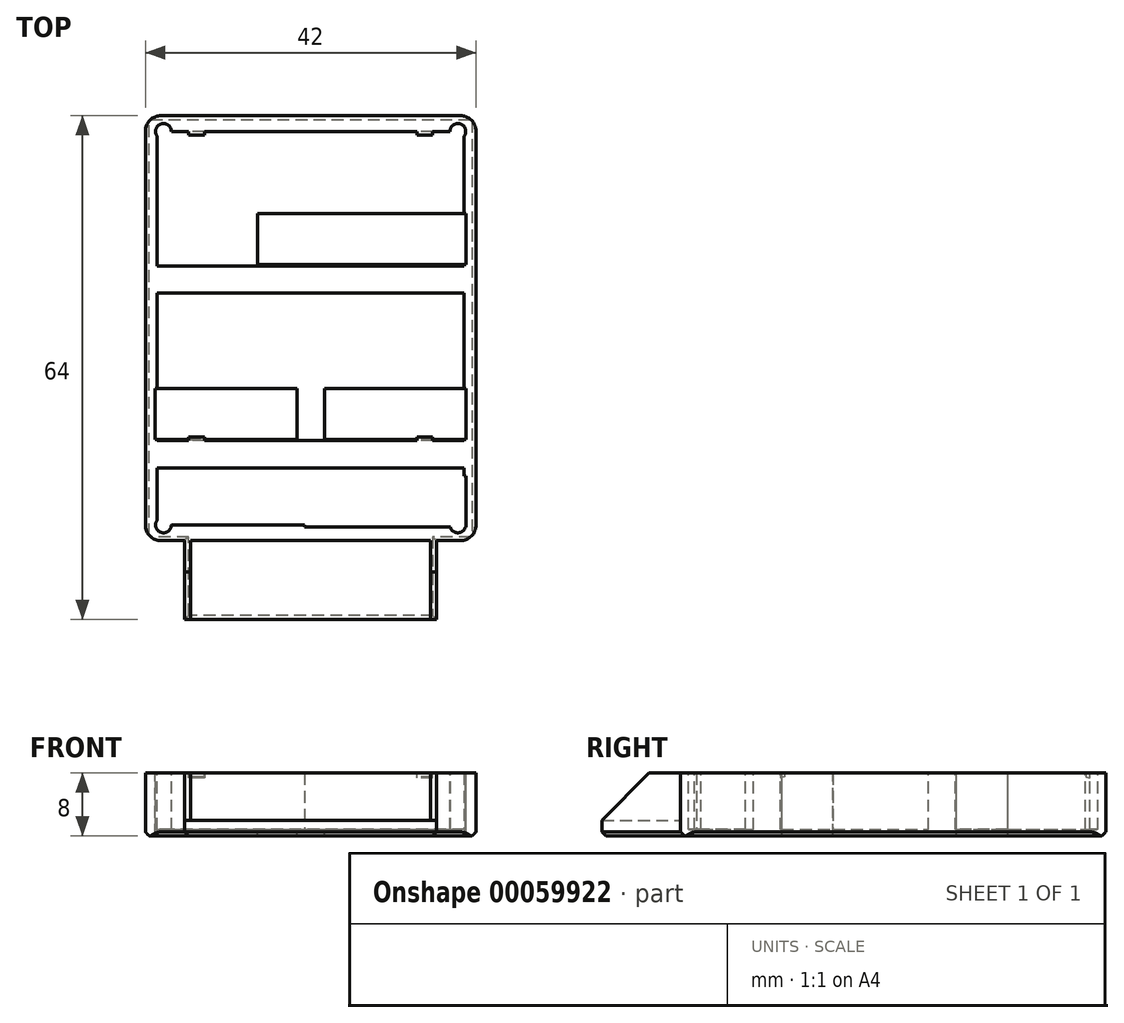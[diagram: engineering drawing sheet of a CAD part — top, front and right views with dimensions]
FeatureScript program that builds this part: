
annotation { "Feature Type Name" : "Feature", "Feature Type Description" : "" }
export const myFeature = defineFeature(function(context is Context, id is Id, definition is map)
    precondition{}
    {
        {
            var Q0;
            Q0=qCreatedBy(makeId("Top.planeOp"),FACE);
            var sketch = newSketch(context, id + "F0", { "sketchPlane" : qUnion([Q0])});
            skLineSegment(sketch, "E0.bottom", {"start": v(-21, 0) * mm, "end": v(21, 0) * mm});
            skLineSegment(sketch, "E0.top", {"start": v(-21, 54) * mm, "end": v(21, 54) * mm});
            skLineSegment(sketch, "E0.left", {"start": v(-21, 0) * mm, "end": v(-21, 54) * mm});
            skLineSegment(sketch, "E0.right", {"start": v(21, 0) * mm, "end": v(21, 54) * mm});
            skSolve(sketch);
        }
        {
            var Q0;
            Q0=makeQuery(id+"F0.imprint","IMPRINT",FACE,{"disambiguationData":[TD([[makeQuery(id+"F0.imprint","IMPRINT",EDGE,{"derivedFrom":sQuery(id+"F0.wireOp",EDGE,"E0.bottom")}),1.0]])]});
            extrude(context, id + "F1", {"entities" : qUnion([Q0]), "depth" : 8 * mm});
        }
        {
            var Q0;
            Q0=makeQuery(id+"F1.opExtrude","CAP_FACE",FACE,{"disambiguationData":[OSD([sQuery(id+"F0.wireOp",EDGE,"E0.bottom"),sQuery(id+"F0.wireOp",EDGE,"E0.top"),sQuery(id+"F0.wireOp",EDGE,"E0.left"),sQuery(id+"F0.wireOp",EDGE,"E0.right")])],"isStart":false});
            var sketch = newSketch(context, id + "F2", { "sketchPlane" : qUnion([Q0])});
            skLineSegment(sketch, "E1.bottom", {"start": v(-19.5, 2) * mm, "end": v(19.5, 2) * mm});
            skLineSegment(sketch, "E1.top", {"start": v(-19.5, 52) * mm, "end": v(19.5, 52) * mm});
            skLineSegment(sketch, "E1.left", {"start": v(-19.5, 2) * mm, "end": v(-19.5, 52) * mm});
            skLineSegment(sketch, "E1.right", {"start": v(19.5, 2) * mm, "end": v(19.5, 52) * mm});
            skLineSegment(sketch, "E2", {"start": v(0, 0) * mm, "end": v(0, 2) * mm, "construction": true});
            skLineSegment(sketch, "E3", {"start": v(21, 27) * mm, "end": v(19.5, 27) * mm, "construction": true});
            skSolve(sketch);
        }
        {
            var Q0;
            Q0 = qSketchRegion(id + "F2", true);
            extrude(context, id + "F3", {"entities" : qUnion([Q0]), "operationType" : NewBodyOperationType.REMOVE, "oppositeDirection" : true, "depth" : 7.2 * mm});
        }
        {
            var Q0;
            Q0=makeQuery(id+"F1.opExtrude","CAP_FACE",FACE,{"disambiguationData":[OSD([sQuery(id+"F0.wireOp",EDGE,"E0.bottom"),sQuery(id+"F0.wireOp",EDGE,"E0.top"),sQuery(id+"F0.wireOp",EDGE,"E0.left"),sQuery(id+"F0.wireOp",EDGE,"E0.right")])],"isStart":false});
            var sketch = newSketch(context, id + "F4", { "sketchPlane" : qUnion([Q0])});
            skPoint(sketch, "E4", {"position": v(-18.7, 52) * mm});
            skPoint(sketch, "E5", {"position": v(18.7, 52) * mm});
            skPoint(sketch, "E6", {"position": v(18.7, 2) * mm});
            skPoint(sketch, "E7", {"position": v(-18.7, 2) * mm});
            skCircle(sketch, "E8", {"center": v(-18.7, 52) * mm, "radius": 1 * mm});
            skCircle(sketch, "E9", {"center": v(18.7, 52) * mm, "radius": 1 * mm});
            skCircle(sketch, "E10", {"center": v(18.7, 2) * mm, "radius": 1 * mm});
            skCircle(sketch, "E11", {"center": v(-18.7, 2) * mm, "radius": 1 * mm});
            skSolve(sketch);
        }
        {
            var Q0;
            {var subQ0=sQuery(id+"F4.wireOp",EDGE,"E8");var subQ1=makeQuery(id+"F3.boolean.opBoolean","COPY",EDGE,{"derivedFrom":makeQuery(id+"F3.opExtrude","CAP_EDGE",EDGE,{"disambiguationData":[OSD([sQuery(id+"F2.wireOp",EDGE,"E1.top")])],"isStart":true})});var subQ2=makeQuery(id+"F4.imprint","INTERSECT",VERTEX,{"derivedFrom":[subQ1,subQ0]});Q0=makeQuery(id+"F4.imprint","IMPRINT",FACE,{"disambiguationData":[TD([[makeQuery(id+"F4.imprint","IMPRINT",EDGE,{"disambiguationData":[TD([[subQ2,-1.0]])],"derivedFrom":subQ0}),1.0]])]});}
            var Q1;
            {var subQ0=sQuery(id+"F4.wireOp",EDGE,"E8");var subQ1=makeQuery(id+"F3.boolean.opBoolean","COPY",EDGE,{"derivedFrom":makeQuery(id+"F3.opExtrude","CAP_EDGE",EDGE,{"disambiguationData":[OSD([sQuery(id+"F2.wireOp",EDGE,"E1.top")])],"isStart":true})});var subQ2=makeQuery(id+"F4.imprint","INTERSECT",VERTEX,{"derivedFrom":[subQ1,subQ0]});Q1=makeQuery(id+"F4.imprint","IMPRINT",FACE,{"disambiguationData":[TD([[makeQuery(id+"F4.imprint","IMPRINT",EDGE,{"disambiguationData":[TD([[subQ2,1.0]])],"derivedFrom":subQ0}),1.0]])]});}
            var Q2;
            {var subQ0=sQuery(id+"F4.wireOp",EDGE,"E9");var subQ1=makeQuery(id+"F3.boolean.opBoolean","COPY",EDGE,{"derivedFrom":makeQuery(id+"F3.opExtrude","CAP_EDGE",EDGE,{"disambiguationData":[OSD([sQuery(id+"F2.wireOp",EDGE,"E1.top")])],"isStart":true})});var subQ2=makeQuery(id+"F4.imprint","INTERSECT",VERTEX,{"derivedFrom":[subQ1,subQ0]});Q2=makeQuery(id+"F4.imprint","IMPRINT",FACE,{"disambiguationData":[TD([[makeQuery(id+"F4.imprint","IMPRINT",EDGE,{"disambiguationData":[TD([[subQ2,-1.0]])],"derivedFrom":subQ0}),1.0]])]});}
            var Q3;
            {var subQ0=sQuery(id+"F4.wireOp",EDGE,"E9");var subQ1=makeQuery(id+"F3.boolean.opBoolean","COPY",EDGE,{"derivedFrom":makeQuery(id+"F3.opExtrude","CAP_EDGE",EDGE,{"disambiguationData":[OSD([sQuery(id+"F2.wireOp",EDGE,"E1.top")])],"isStart":true})});var subQ2=makeQuery(id+"F4.imprint","INTERSECT",VERTEX,{"derivedFrom":[subQ1,subQ0]});Q3=makeQuery(id+"F4.imprint","IMPRINT",FACE,{"disambiguationData":[TD([[makeQuery(id+"F4.imprint","IMPRINT",EDGE,{"disambiguationData":[TD([[subQ2,1.0]])],"derivedFrom":subQ0}),1.0]])]});}
            var Q4;
            {var subQ0=sQuery(id+"F4.wireOp",EDGE,"E10");var subQ1=makeQuery(id+"F3.boolean.opBoolean","COPY",EDGE,{"derivedFrom":makeQuery(id+"F3.opExtrude","CAP_EDGE",EDGE,{"disambiguationData":[OSD([sQuery(id+"F2.wireOp",EDGE,"E1.bottom")])],"isStart":true})});var subQ2=makeQuery(id+"F4.imprint","INTERSECT",VERTEX,{"derivedFrom":[subQ1,subQ0]});Q4=makeQuery(id+"F4.imprint","IMPRINT",FACE,{"disambiguationData":[TD([[makeQuery(id+"F4.imprint","IMPRINT",EDGE,{"disambiguationData":[TD([[subQ2,1.0]])],"derivedFrom":subQ0}),1.0]])]});}
            var Q5;
            {var subQ0=sQuery(id+"F4.wireOp",EDGE,"E11");var subQ1=makeQuery(id+"F3.boolean.opBoolean","COPY",EDGE,{"derivedFrom":makeQuery(id+"F3.opExtrude","CAP_EDGE",EDGE,{"disambiguationData":[OSD([sQuery(id+"F2.wireOp",EDGE,"E1.bottom")])],"isStart":true})});var subQ2=makeQuery(id+"F4.imprint","INTERSECT",VERTEX,{"derivedFrom":[subQ1,subQ0]});Q5=makeQuery(id+"F4.imprint","IMPRINT",FACE,{"disambiguationData":[TD([[makeQuery(id+"F4.imprint","IMPRINT",EDGE,{"disambiguationData":[TD([[subQ2,-1.0]])],"derivedFrom":subQ0}),1.0]])]});}
            var Q6;
            {var subQ0=sQuery(id+"F4.wireOp",EDGE,"E11");var subQ1=makeQuery(id+"F3.boolean.opBoolean","COPY",EDGE,{"derivedFrom":makeQuery(id+"F3.opExtrude","CAP_EDGE",EDGE,{"disambiguationData":[OSD([sQuery(id+"F2.wireOp",EDGE,"E1.bottom")])],"isStart":true})});var subQ2=makeQuery(id+"F4.imprint","INTERSECT",VERTEX,{"derivedFrom":[subQ1,subQ0]});Q6=makeQuery(id+"F4.imprint","IMPRINT",FACE,{"disambiguationData":[TD([[makeQuery(id+"F4.imprint","IMPRINT",EDGE,{"disambiguationData":[TD([[subQ2,1.0]])],"derivedFrom":subQ0}),1.0]])]});}
            var Q7;
            {var subQ0=sQuery(id+"F4.wireOp",EDGE,"E10");var subQ1=makeQuery(id+"F3.boolean.opBoolean","COPY",EDGE,{"derivedFrom":makeQuery(id+"F3.opExtrude","CAP_EDGE",EDGE,{"disambiguationData":[OSD([sQuery(id+"F2.wireOp",EDGE,"E1.bottom")])],"isStart":true})});var subQ2=makeQuery(id+"F4.imprint","INTERSECT",VERTEX,{"derivedFrom":[subQ1,subQ0]});Q7=makeQuery(id+"F4.imprint","IMPRINT",FACE,{"disambiguationData":[TD([[makeQuery(id+"F4.imprint","IMPRINT",EDGE,{"disambiguationData":[TD([[subQ2,-1.0]])],"derivedFrom":subQ0}),1.0]])]});}
            var Q8;
            Q8=makeQuery(id+"F3.boolean.opBoolean","COPY",FACE,{"derivedFrom":makeQuery(id+"F3.opExtrude","CAP_FACE",FACE,{"disambiguationData":[OSD([sQuery(id+"F2.wireOp",EDGE,"E1.bottom"),sQuery(id+"F2.wireOp",EDGE,"E1.top"),sQuery(id+"F2.wireOp",EDGE,"E1.left"),sQuery(id+"F2.wireOp",EDGE,"E1.right")])],"isStart":false})});
            extrude(context, id + "F5", {"entities" : qUnion([Q0, Q1, Q2, Q3, Q4, Q5, Q6, Q7]), "operationType" : NewBodyOperationType.REMOVE, "endBound" : BoundingType.UP_TO_SURFACE, "oppositeDirection" : true, "endBoundEntityFace" : qUnion([Q8]), "depth" : 25 * mm});
        }
        {
            var Q0;
            Q0=makeQuery(id+"F1.opExtrude","CAP_FACE",FACE,{"disambiguationData":[OSD([sQuery(id+"F0.wireOp",EDGE,"E0.bottom"),sQuery(id+"F0.wireOp",EDGE,"E0.top"),sQuery(id+"F0.wireOp",EDGE,"E0.left"),sQuery(id+"F0.wireOp",EDGE,"E0.right")])],"isStart":false});
            var sketch = newSketch(context, id + "F6", { "sketchPlane" : qUnion([Q0])});
            skLineSegment(sketch, "E12.bottom", {"start": v(-0.75, 8.25) * mm, "end": v(19.75, 8.25) * mm});
            skLineSegment(sketch, "E12.top", {"start": v(-0.75, 1.75) * mm, "end": v(19.75, 1.75) * mm});
            skLineSegment(sketch, "E12.left", {"start": v(-0.75, 8.25) * mm, "end": v(-0.75, 1.75) * mm});
            skLineSegment(sketch, "E12.right", {"start": v(19.75, 8.25) * mm, "end": v(19.75, 1.75) * mm});
            skLineSegment(sketch, "E13.bottom", {"start": v(19.75, 12.85) * mm, "end": v(1.75, 12.85) * mm});
            skLineSegment(sketch, "E13.top", {"start": v(19.75, 19.35) * mm, "end": v(1.75, 19.35) * mm});
            skLineSegment(sketch, "E13.left", {"start": v(19.75, 12.85) * mm, "end": v(19.75, 19.35) * mm});
            skLineSegment(sketch, "E13.right", {"start": v(1.75, 12.85) * mm, "end": v(1.75, 19.35) * mm});
            skLineSegment(sketch, "E14", {"start": v(19.75, 8.25) * mm, "end": v(19.75, 12.85) * mm, "construction": true});
            skLineSegment(sketch, "E15", {"start": v(0, 0) * mm, "end": v(0, 22.3) * mm, "construction": true});
            skLineSegment(sketch, "E16.MirrorCS", {"start": v(-19.75, 12.85) * mm, "end": v(-1.75, 12.85) * mm});
            skLineSegment(sketch, "E17.MirrorCS", {"start": v(-19.75, 19.35) * mm, "end": v(-1.75, 19.35) * mm});
            skLineSegment(sketch, "E18.MirrorCS", {"start": v(-19.75, 12.85) * mm, "end": v(-19.75, 19.35) * mm});
            skLineSegment(sketch, "E19.MirrorCS", {"start": v(-1.75, 12.85) * mm, "end": v(-1.75, 19.35) * mm});
            skLineSegment(sketch, "E20.bottom", {"start": v(19.75, 41.55) * mm, "end": v(-6.75, 41.55) * mm});
            skLineSegment(sketch, "E20.top", {"start": v(19.75, 35.05) * mm, "end": v(-6.75, 35.05) * mm});
            skLineSegment(sketch, "E20.left", {"start": v(19.75, 41.55) * mm, "end": v(19.75, 35.05) * mm});
            skLineSegment(sketch, "E20.right", {"start": v(-6.75, 41.55) * mm, "end": v(-6.75, 35.05) * mm});
            skLineSegment(sketch, "E21", {"start": v(19.75, 19.35) * mm, "end": v(19.75, 35.05) * mm, "construction": true});
            skSolve(sketch);
        }
        {
            var Q0;
            Q0 = qSketchRegion(id + "F6", true);
            extrude(context, id + "F7", {"entities" : qUnion([Q0]), "operationType" : NewBodyOperationType.REMOVE, "endBound" : BoundingType.THROUGH_ALL, "oppositeDirection" : true, "depth" : 25 * mm});
        }
        {
            var Q0;
            Q0=makeQuery(id+"F1.opExtrude","SWEPT_FACE",FACE,{"disambiguationData":[OSD([sQuery(id+"F0.wireOp",EDGE,"E0.bottom")])]});
            var sketch = newSketch(context, id + "F8", { "sketchPlane" : qUnion([Q0])});
            skLineSegment(sketch, "E22", {"start": v(-15.25, 8) * mm, "end": v(-15.25, 2) * mm});
            skLineSegment(sketch, "E23", {"start": v(-15.25, 2) * mm, "end": v(15.25, 2) * mm});
            skLineSegment(sketch, "E24", {"start": v(15.25, 2) * mm, "end": v(15.25, 8) * mm});
            skLineSegment(sketch, "E25", {"start": v(0, 0) * mm, "end": v(0, 2) * mm, "construction": true});
            skLineSegment(sketch, "E26", {"start": v(-15.25, 8) * mm, "end": v(-16, 8) * mm});
            skLineSegment(sketch, "E27", {"start": v(-16, 8) * mm, "end": v(-16, 0) * mm});
            skLineSegment(sketch, "E28", {"start": v(-16, 0) * mm, "end": v(16, 0) * mm});
            skLineSegment(sketch, "E29", {"start": v(16, 0) * mm, "end": v(16, 8) * mm});
            skLineSegment(sketch, "E30", {"start": v(16, 8) * mm, "end": v(15.25, 8) * mm});
            skSolve(sketch);
        }
        {
            var Q0;
            Q0 = qSketchRegion(id + "F8", true);
            extrude(context, id + "F9", {"entities" : qUnion([Q0]), "operationType" : NewBodyOperationType.ADD, "depth" : 10 * mm});
        }
        {
            var Q0;
            Q0=makeQuery(id+"F9.opExtrude","SWEPT_EDGE",EDGE,{"disambiguationData":[OSD([sQuery(id+"F0.wireOp",EDGE,"E0.bottom"),sQuery(id+"F8.wireOp",EDGE,"E28"),sQuery(id+"F8.wireOp",EDGE,"E29")])]});
            var Q1;
            {var subQ0=sQuery(id+"F0.wireOp",EDGE,"E0.right");var subQ1=sQuery(id+"F0.wireOp",EDGE,"E0.bottom");Q1=makeQuery(id+"F9.boolean.opBoolean","SPLIT",EDGE,{"disambiguationData":[TD([makeQuery(id+"F1.opExtrude","SWEPT_FACE",FACE,{"disambiguationData":[OSD([subQ0])]})])],"derivedFrom":makeQuery(id+"F1.opExtrude","CAP_EDGE",EDGE,{"disambiguationData":[OSD([subQ1])],"isStart":true})});}
            var Q2;
            Q2=makeQuery(id+"F1.opExtrude","CAP_EDGE",EDGE,{"disambiguationData":[OSD([sQuery(id+"F0.wireOp",EDGE,"E0.right")])],"isStart":true});
            var Q3;
            Q3=makeQuery(id+"F9.opExtrude","SWEPT_EDGE",EDGE,{"disambiguationData":[OSD([sQuery(id+"F0.wireOp",EDGE,"E0.bottom"),sQuery(id+"F8.wireOp",EDGE,"E27"),sQuery(id+"F8.wireOp",EDGE,"E28")])]});
            var Q4;
            {var subQ0=sQuery(id+"F0.wireOp",EDGE,"E0.left");var subQ1=sQuery(id+"F0.wireOp",EDGE,"E0.bottom");Q4=makeQuery(id+"F9.boolean.opBoolean","SPLIT",EDGE,{"disambiguationData":[TD([makeQuery(id+"F1.opExtrude","SWEPT_FACE",FACE,{"disambiguationData":[OSD([subQ0])]})])],"derivedFrom":makeQuery(id+"F1.opExtrude","CAP_EDGE",EDGE,{"disambiguationData":[OSD([subQ1])],"isStart":true})});}
            var Q5;
            Q5=makeQuery(id+"F1.opExtrude","CAP_EDGE",EDGE,{"disambiguationData":[OSD([sQuery(id+"F0.wireOp",EDGE,"E0.left")])],"isStart":true});
            var Q6;
            Q6=makeQuery(id+"F1.opExtrude","CAP_EDGE",EDGE,{"disambiguationData":[OSD([sQuery(id+"F0.wireOp",EDGE,"E0.top")])],"isStart":true});
            var Q7;
            Q7=makeQuery(id+"F9.opExtrude","CAP_EDGE",EDGE,{"disambiguationData":[OSD([sQuery(id+"F8.wireOp",EDGE,"E28")])],"isStart":false});
            chamfer(context, id + "F10", {"entities" : qUnion([Q0, Q1, Q2, Q3, Q4, Q5, Q6, Q7]), "width" : 0.5 * mm, "tangentPropagation" : true});
        }
        {
            var Q0;
            Q0=makeQuery(id+"F1.opExtrude","SWEPT_EDGE",EDGE,{"disambiguationData":[OSD([sQuery(id+"F0.wireOp",EDGE,"E0.bottom"),sQuery(id+"F0.wireOp",EDGE,"E0.right")])]});
            var Q1;
            Q1=makeQuery(id+"F1.opExtrude","SWEPT_EDGE",EDGE,{"disambiguationData":[OSD([sQuery(id+"F0.wireOp",EDGE,"E0.top"),sQuery(id+"F0.wireOp",EDGE,"E0.right")])]});
            var Q2;
            Q2=makeQuery(id+"F1.opExtrude","SWEPT_EDGE",EDGE,{"disambiguationData":[OSD([sQuery(id+"F0.wireOp",EDGE,"E0.bottom"),sQuery(id+"F0.wireOp",EDGE,"E0.left")])]});
            var Q3;
            Q3=makeQuery(id+"F1.opExtrude","SWEPT_EDGE",EDGE,{"disambiguationData":[OSD([sQuery(id+"F0.wireOp",EDGE,"E0.top"),sQuery(id+"F0.wireOp",EDGE,"E0.left")])]});
            fillet(context, id + "F11", {"entities" : qUnion([Q0, Q1, Q2, Q3]), "radius" : 2 * mm, "tangentPropagation" : true, "allowEdgeOverflow" : false});
        }
        {
            var Q0;
            Q0=makeQuery(id+"F9.boolean.opBoolean","MERGE",FACE,{"derivedFrom":[makeQuery(id+"F1.opExtrude","CAP_FACE",FACE,{"disambiguationData":[OSD([sQuery(id+"F0.wireOp",EDGE,"E0.bottom"),sQuery(id+"F0.wireOp",EDGE,"E0.top"),sQuery(id+"F0.wireOp",EDGE,"E0.left"),sQuery(id+"F0.wireOp",EDGE,"E0.right")])],"isStart":false}),makeQuery(id+"F9.opExtrude","SWEPT_FACE",FACE,{"disambiguationData":[OSD([sQuery(id+"F8.wireOp",EDGE,"E26")])]}),makeQuery(id+"F9.opExtrude","SWEPT_FACE",FACE,{"disambiguationData":[OSD([sQuery(id+"F8.wireOp",EDGE,"E30")])]})]});
            var sketch = newSketch(context, id + "F12", { "sketchPlane" : qUnion([Q0])});
            skLineSegment(sketch, "E31.bottom", {"start": v(-19.5, 9.25) * mm, "end": v(19.5, 9.25) * mm});
            skLineSegment(sketch, "E31.top", {"start": v(-19.5, 12.7) * mm, "end": v(19.5, 12.7) * mm});
            skLineSegment(sketch, "E31.left", {"start": v(-19.5, 9.25) * mm, "end": v(-19.5, 12.7) * mm});
            skLineSegment(sketch, "E31.right", {"start": v(19.5, 9.25) * mm, "end": v(19.5, 12.7) * mm});
            skLineSegment(sketch, "E32.bottom", {"start": v(19.5, 34.9) * mm, "end": v(-19.5, 34.9) * mm});
            skLineSegment(sketch, "E32.top", {"start": v(19.5, 31.45) * mm, "end": v(-19.5, 31.45) * mm});
            skLineSegment(sketch, "E32.left", {"start": v(19.5, 34.9) * mm, "end": v(19.5, 31.45) * mm});
            skLineSegment(sketch, "E32.right", {"start": v(-19.5, 34.9) * mm, "end": v(-19.5, 31.45) * mm});
            skSolve(sketch);
        }
        {
            var Q0;
            Q0=makeQuery(id+"F12.imprint","IMPRINT",FACE,{"disambiguationData":[TD([[makeQuery(id+"F12.imprint","IMPRINT",EDGE,{"derivedFrom":sQuery(id+"F12.wireOp",EDGE,"E31.bottom")}),1.0]])]});
            var Q1;
            Q1=makeQuery(id+"F12.imprint","IMPRINT",FACE,{"disambiguationData":[TD([[makeQuery(id+"F12.imprint","IMPRINT",EDGE,{"derivedFrom":sQuery(id+"F12.wireOp",EDGE,"E32.bottom")}),1.0]])]});
            var Q2;
            {var subQ0=sQuery(id+"F2.wireOp",EDGE,"E1.bottom");var subQ1=sQuery(id+"F4.wireOp",EDGE,"E8");var subQ2=sQuery(id+"F2.wireOp",EDGE,"E1.top");var subQ3=sQuery(id+"F4.wireOp",EDGE,"E11");var subQ4=sQuery(id+"F2.wireOp",EDGE,"E1.left");var subQ5=sQuery(id+"F4.wireOp",EDGE,"E9");var subQ6=sQuery(id+"F2.wireOp",EDGE,"E1.right");Q2=makeQuery(id+"F7.boolean.opBoolean","SPLIT",FACE,{"disambiguationData":[TD([makeQuery(id+"F3.boolean.opBoolean","COPY",FACE,{"derivedFrom":makeQuery(id+"F3.opExtrude","SWEPT_FACE",FACE,{"disambiguationData":[OSD([subQ0])]})})])],"derivedFrom":makeQuery(id+"F5.boolean.opBoolean","MERGE",FACE,{"derivedFrom":[makeQuery(id+"F3.boolean.opBoolean","COPY",FACE,{"derivedFrom":makeQuery(id+"F3.opExtrude","CAP_FACE",FACE,{"disambiguationData":[OSD([subQ0,subQ2,subQ4,subQ6])],"isStart":false})}),makeQuery(id+"F5.opExtrude","CAP_FACE",FACE,{"disambiguationData":[OSD([subQ1])],"isStart":false}),makeQuery(id+"F5.opExtrude","CAP_FACE",FACE,{"disambiguationData":[OSD([subQ5])],"isStart":false}),makeQuery(id+"F5.opExtrude","CAP_FACE",FACE,{"disambiguationData":[OSD([sQuery(id+"F4.wireOp",EDGE,"E10")])],"isStart":false}),makeQuery(id+"F5.opExtrude","CAP_FACE",FACE,{"disambiguationData":[OSD([subQ3])],"isStart":false})]})});}
            extrude(context, id + "F13", {"entities" : qUnion([Q0, Q1]), "operationType" : NewBodyOperationType.ADD, "endBound" : BoundingType.UP_TO_SURFACE, "oppositeDirection" : true, "endBoundEntityFace" : qUnion([Q2]), "offsetDistance" : 25 * mm, "depth" : 25 * mm});
        }
        {
            var Q0;
            {var subQ2=sQuery(id+"F4.wireOp",EDGE,"E8");var subQ3=makeQuery(id+"F5.boolean.opBoolean","COPY",FACE,{"derivedFrom":makeQuery(id+"F5.opExtrude","SWEPT_FACE",FACE,{"disambiguationData":[OSD([subQ2])]})});var subQ6=sQuery(id+"F2.wireOp",EDGE,"E1.left");Q0=makeQuery(id+"F13.boolean.opBoolean","SPLIT",FACE,{"disambiguationData":[TD([subQ3])],"derivedFrom":makeQuery(id+"F7.boolean.opBoolean","SPLIT",FACE,{"disambiguationData":[TD([subQ3])],"derivedFrom":makeQuery(id+"F3.boolean.opBoolean","COPY",FACE,{"derivedFrom":makeQuery(id+"F3.opExtrude","SWEPT_FACE",FACE,{"disambiguationData":[OSD([subQ6])]})})})});}
            cPlane(context, id + "F14", {"entities" : qUnion([Q0]), "cplaneType" : CPlaneType.OFFSET, "offset" : 5 * mm, "width" : 150 * mm, "height" : 150 * mm});
        }
        {
            var Q0;
            Q0=qCreatedBy(id+"F14.planeOp",FACE);
            var sketch = newSketch(context, id + "F15", { "sketchPlane" : qUnion([Q0])});
            skLineSegment(sketch, "E33", {"start": v(12.7, 8) * mm, "end": v(13.2, 8) * mm});
            skLineSegment(sketch, "E34", {"start": v(13.2, 8) * mm, "end": v(13.2, 7.5) * mm});
            skLineSegment(sketch, "E35", {"start": v(13.2, 7.5) * mm, "end": v(12.7, 7.37) * mm});
            skLineSegment(sketch, "E36", {"start": v(12.7, 7.37) * mm, "end": v(12.7, 8) * mm});
            skLineSegment(sketch, "E37", {"start": v(52, 8) * mm, "end": v(51.5, 8) * mm});
            skLineSegment(sketch, "E38", {"start": v(51.5, 8) * mm, "end": v(51.5, 7.5) * mm});
            skLineSegment(sketch, "E39", {"start": v(51.5, 7.5) * mm, "end": v(52, 7.37) * mm});
            skLineSegment(sketch, "E40", {"start": v(52, 7.37) * mm, "end": v(52, 8) * mm});
            skSolve(sketch);
        }
        {
            var Q0;
            Q0 = qSketchRegion(id + "F15", true);
            extrude(context, id + "F16", {"entities" : qUnion([Q0]), "operationType" : NewBodyOperationType.ADD, "endBound" : BoundingType.SYMMETRIC, "depth" : 2 * mm});
        }
        {
            var Q0;
            Q0=qCreatedBy(id+"F14.planeOp",FACE);
            cPlane(context, id + "F17", {"entities" : qUnion([Q0]), "cplaneType" : CPlaneType.OFFSET, "offset" : 29 * mm, "width" : 150 * mm, "height" : 150 * mm});
        }
        {
            var Q0;
            Q0=qCreatedBy(id+"F17.planeOp",FACE);
            var sketch = newSketch(context, id + "F18", { "sketchPlane" : qUnion([Q0])});
            skLineSegment(sketch, "E41.0.0", {"start": v(13.2, 8) * mm, "end": v(12.7, 8) * mm});
            skLineSegment(sketch, "E41.0.1", {"start": v(12.7, 8) * mm, "end": v(12.7, 7.37) * mm});
            skLineSegment(sketch, "E41.0.2", {"start": v(12.7, 7.37) * mm, "end": v(13.2, 7.5) * mm});
            skLineSegment(sketch, "E41.0.3", {"start": v(13.2, 7.5) * mm, "end": v(13.2, 8) * mm});
            skLineSegment(sketch, "E42.0.0", {"start": v(52, 7.37) * mm, "end": v(52, 8) * mm});
            skLineSegment(sketch, "E42.0.1", {"start": v(52, 8) * mm, "end": v(51.5, 8) * mm});
            skLineSegment(sketch, "E42.0.2", {"start": v(51.5, 8) * mm, "end": v(51.5, 7.5) * mm});
            skLineSegment(sketch, "E42.0.3", {"start": v(51.5, 7.5) * mm, "end": v(52, 7.37) * mm});
            skSolve(sketch);
        }
        {
            var Q0;
            Q0 = qSketchRegion(id + "F18", true);
            extrude(context, id + "F19", {"entities" : qUnion([Q0]), "operationType" : NewBodyOperationType.ADD, "endBound" : BoundingType.SYMMETRIC, "depth" : 2 * mm});
        }
        {
            var Q0;
            Q0=makeQuery(id+"F9.opExtrude","CAP_EDGE",EDGE,{"disambiguationData":[OSD([sQuery(id+"F8.wireOp",EDGE,"E26")])],"isStart":false});
            var Q1;
            Q1=makeQuery(id+"F9.opExtrude","CAP_EDGE",EDGE,{"disambiguationData":[OSD([sQuery(id+"F8.wireOp",EDGE,"E30")])],"isStart":false});
            chamfer(context, id + "F20", {"entities" : qUnion([Q0, Q1]), "width" : 6 * mm, "tangentPropagation" : true});
        }
        {
            var Q0;
            Q0=makeQuery(id+"F9.boolean.opBoolean","MERGE",FACE,{"derivedFrom":[makeQuery(id+"F1.opExtrude","CAP_FACE",FACE,{"disambiguationData":[OSD([sQuery(id+"F0.wireOp",EDGE,"E0.bottom"),sQuery(id+"F0.wireOp",EDGE,"E0.top"),sQuery(id+"F0.wireOp",EDGE,"E0.left"),sQuery(id+"F0.wireOp",EDGE,"E0.right")])],"isStart":true}),makeQuery(id+"F9.opExtrude","SWEPT_FACE",FACE,{"disambiguationData":[OSD([sQuery(id+"F8.wireOp",EDGE,"E28")])]})]});
            var sketch = newSketch(context, id + "F21", { "sketchPlane" : qUnion([Q0])});
            skLineSegment(sketch, "E43.bottom", {"start": v(-19.75, -19.35) * mm, "end": v(-1.75, -19.35) * mm});
            skLineSegment(sketch, "E43.top", {"start": v(-19.75, -12.85) * mm, "end": v(-1.75, -12.85) * mm});
            skLineSegment(sketch, "E43.left", {"start": v(-19.75, -19.35) * mm, "end": v(-19.75, -12.85) * mm});
            skLineSegment(sketch, "E43.right", {"start": v(-1.75, -19.35) * mm, "end": v(-1.75, -12.85) * mm});
            skLineSegment(sketch, "E44.bottom", {"start": v(1.75, -19.35) * mm, "end": v(19.75, -19.35) * mm});
            skLineSegment(sketch, "E44.top", {"start": v(1.75, -12.85) * mm, "end": v(19.75, -12.85) * mm});
            skLineSegment(sketch, "E44.left", {"start": v(1.75, -19.35) * mm, "end": v(1.75, -12.85) * mm});
            skLineSegment(sketch, "E44.right", {"start": v(19.75, -19.35) * mm, "end": v(19.75, -12.85) * mm});
            skSolve(sketch);
        }
        {
            var Q0;
            Q0=makeQuery(id+"F9.boolean.opBoolean","MERGE",FACE,{"derivedFrom":[makeQuery(id+"F1.opExtrude","CAP_FACE",FACE,{"disambiguationData":[OSD([sQuery(id+"F0.wireOp",EDGE,"E0.bottom"),sQuery(id+"F0.wireOp",EDGE,"E0.top"),sQuery(id+"F0.wireOp",EDGE,"E0.left"),sQuery(id+"F0.wireOp",EDGE,"E0.right")])],"isStart":true}),makeQuery(id+"F9.opExtrude","SWEPT_FACE",FACE,{"disambiguationData":[OSD([sQuery(id+"F8.wireOp",EDGE,"E28")])]})]});
            var sketch = newSketch(context, id + "F22", { "sketchPlane" : qUnion([Q0])});
            skLineSegment(sketch, "E45.bottom", {"start": v(-0.75, -8.25) * mm, "end": v(19.75, -8.25) * mm});
            skLineSegment(sketch, "E45.top", {"start": v(-0.75, -1.75) * mm, "end": v(19.75, -1.75) * mm});
            skLineSegment(sketch, "E45.left", {"start": v(-0.75, -8.25) * mm, "end": v(-0.75, -1.75) * mm});
            skLineSegment(sketch, "E45.right", {"start": v(19.75, -8.25) * mm, "end": v(19.75, -1.75) * mm});
            skSolve(sketch);
        }
        {
            var Q0;
            Q0 = qSketchRegion(id + "F22", true);
            extrude(context, id + "F23", {"entities" : qUnion([Q0]), "operationType" : NewBodyOperationType.ADD, "oppositeDirection" : true, "depth" : 0.8 * mm});
        }
    });
